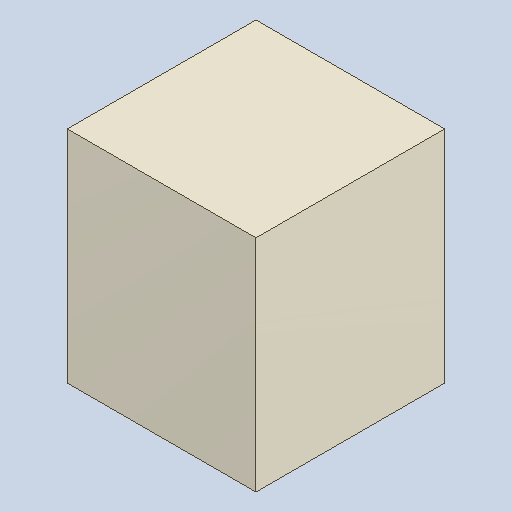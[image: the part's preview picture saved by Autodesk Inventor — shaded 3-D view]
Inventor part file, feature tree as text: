
AUTODESK INVENTOR PART (.ipt)
format: ipt  version: 2023.4 (Build 274418000, 418)  size: 82,944 bytes
history: native  units: mm
features: extrude x1
ambient origin geometry x8: Origin, YZ Plane, XZ Plane, XY Plane, X Axis, Y Axis, Z Axis, Center Point
bodies: Solid1 (feature_tree)
feature tree (1):
  extrude  "Extruded_28"  [1 undecoded]
note: 1 required parameter value undecoded (feature->parameter linkage not recoverable at this tier; creation-order binding heuristic only, values carry confidence <= 0.55)
